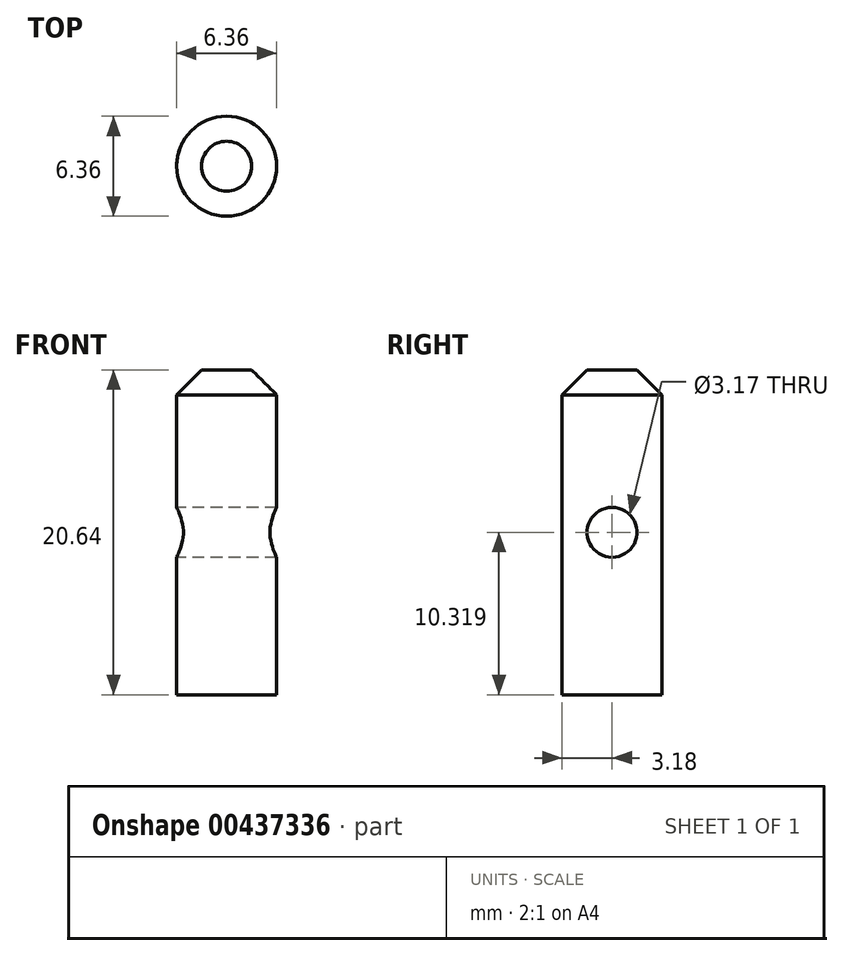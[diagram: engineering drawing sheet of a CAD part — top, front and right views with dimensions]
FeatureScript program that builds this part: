
annotation { "Feature Type Name" : "Feature", "Feature Type Description" : "" }
export const myFeature = defineFeature(function(context is Context, id is Id, definition is map)
    precondition{}
    {
        {
            var Q0;
            Q0=qCreatedBy(makeId("Top.planeOp"),FACE);
            var sketch = newSketch(context, id + "F0", { "sketchPlane" : qUnion([Q0])});
            skCircle(sketch, "E0", {"center": v(0, 0) * mm, "radius": 3.18 * mm});
            skSolve(sketch);
        }
        {
            var Q0;
            Q0=makeQuery(id+"F0.imprint","IMPRINT",FACE,{"disambiguationData":[TD([[makeQuery(id+"F0.imprint","IMPRINT",EDGE,{"derivedFrom":sQuery(id+"F0.wireOp",EDGE,"E0")}),1.0]])]});
            extrude(context, id + "F1", {"entities" : qUnion([Q0]), "depth" : 20.64 * mm});
        }
        {
            var Q0;
            Q0=makeQuery(id+"F1.opExtrude","CAP_EDGE",EDGE,{"disambiguationData":[OSD([sQuery(id+"F0.wireOp",EDGE,"E0")])],"isStart":false});
            chamfer(context, id + "F2", {"entities" : qUnion([Q0]), "width" : 1.59 * mm, "tangentPropagation" : true});
        }
        {
            var Q0;
            Q0=qCreatedBy(makeId("Right.planeOp"),FACE);
            var sketch = newSketch(context, id + "F3", { "sketchPlane" : qUnion([Q0])});
            skCircle(sketch, "E1", {"center": v(0, 10.32) * mm, "radius": 1.59 * mm});
            skSolve(sketch);
        }
        {
            var Q0;
            Q0=qSketchRegion(id+"F3",true);
            extrude(context, id + "F4", {"entities" : qUnion([Q0]), "operationType" : NewBodyOperationType.REMOVE, "endBound" : BoundingType.SYMMETRIC, "depth" : 25.4 * mm});
        }
    });
